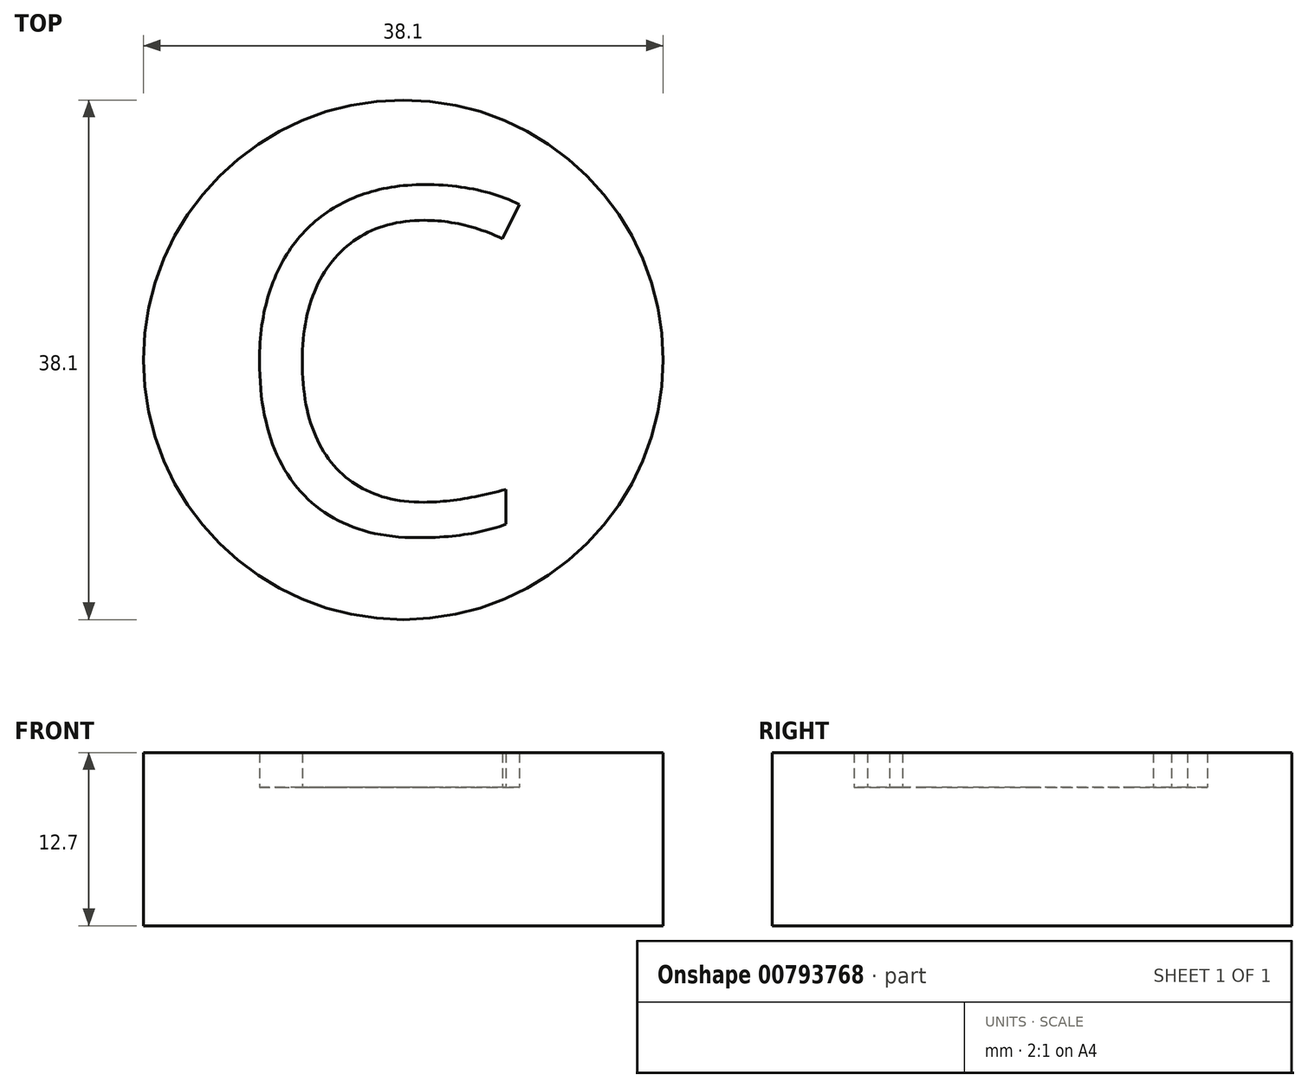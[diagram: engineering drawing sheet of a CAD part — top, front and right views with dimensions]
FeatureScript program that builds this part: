
annotation { "Feature Type Name" : "Feature", "Feature Type Description" : "" }
export const myFeature = defineFeature(function(context is Context, id is Id, definition is map)
    precondition{}
    {
        {
            var Q0;
            Q0=qCreatedBy(makeId("Top.planeOp"),FACE);
            var sketch = newSketch(context, id + "F0", { "sketchPlane" : qUnion([Q0])});
            skCircle(sketch, "E0", {"center": v(0, 0) * mm, "radius": 19.05 * mm});
            skSolve(sketch);
        }
        {
            var Q0;
            Q0 = qSketchRegion(id + "F0", true);
            extrude(context, id + "F1", {"entities" : qUnion([Q0]), "depth" : 12.7 * mm, "offsetDistance" : 25.4 * mm});
        }
        {
            var Q0;
            Q0=qCreatedBy(makeId("Top.planeOp"),FACE);
            var sketch = newSketch(context, id + "F2", { "sketchPlane" : qUnion([Q0])});
            skText(sketch, "E1", { "text": "C", "fontName": "OpenSans-Regular.ttf"});
            const initialGuessF2  = {"E1": [-0.0127, -0.0127, 1, 0, 0.0254]};
            skSetInitialGuess(sketch, initialGuessF2);
            skSolve(sketch);
        }
        {
            var Q0;
            Q0 = qSketchRegion(id + "F2", true);
            extrude(context, id + "F3", {"entities" : qUnion([Q0]), "operationType" : NewBodyOperationType.REMOVE, "depth" : 12.7 * mm, "offsetDistance" : 25.4 * mm, "hasSecondDirection" : true, "secondDirectionOppositeDirection" : false, "secondDirectionDepth" : 10.16 * mm});
        }
    });
